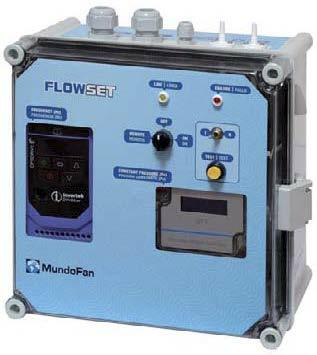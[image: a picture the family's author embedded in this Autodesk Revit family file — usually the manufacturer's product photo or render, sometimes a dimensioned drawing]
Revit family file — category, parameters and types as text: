
# Revit family: FLOWSET-75_VE10849
name_source: partatom
category: Aparatos eléctricos
revit_build: Autodesk Revit 2016 (Build: 20150220_1215(x64)
units: mm (PartAtom-declared; Revit-internal decimal feet)

## family parameters
Compartido = No
Corte con vacíos al cargar = No
Cota de conector redondo = Diámetro de uso
Mantener orientación de anotación = No
Número OmniClass = 23.80.00.00
Punto de cálculo de habitación = No
Se basa en plano de trabajo = No
Siempre vertical = Sí
Tipo de pieza = Caja de conexiones
Título OmniClass = Electric Power and Lighting

## types (1)
- FLOWSET
    Alimentación = 400Vac trifásico
    Corriente = 18 A
    Costo = 0 $
    Código de montaje = VE10849
    Descripción = CONTROL EFICIENCIA ENERGETICA PARA VENTILADORES - Caudal aire constante
    Dimensiones máx. = 270x300x170 mm
    Fabricante = SALVADOR ESCODA
    Imagen de tipo = flowset.jpg
    Leds = linea / fallo
    Modelo = FLOWSET 7,5kW
    Normativas = EN-ISO 14644-1:2000
    Potencia = 7,5 kW
    Regulación = Mediante sonda analógica de presión
    Salida = 400Vac trifásico
    Selector = 3 posiciones remoto / off / on
    URL = www.salvadorescoda.com
    Visualización = frecuencia (Hz) y presión (Pa)
